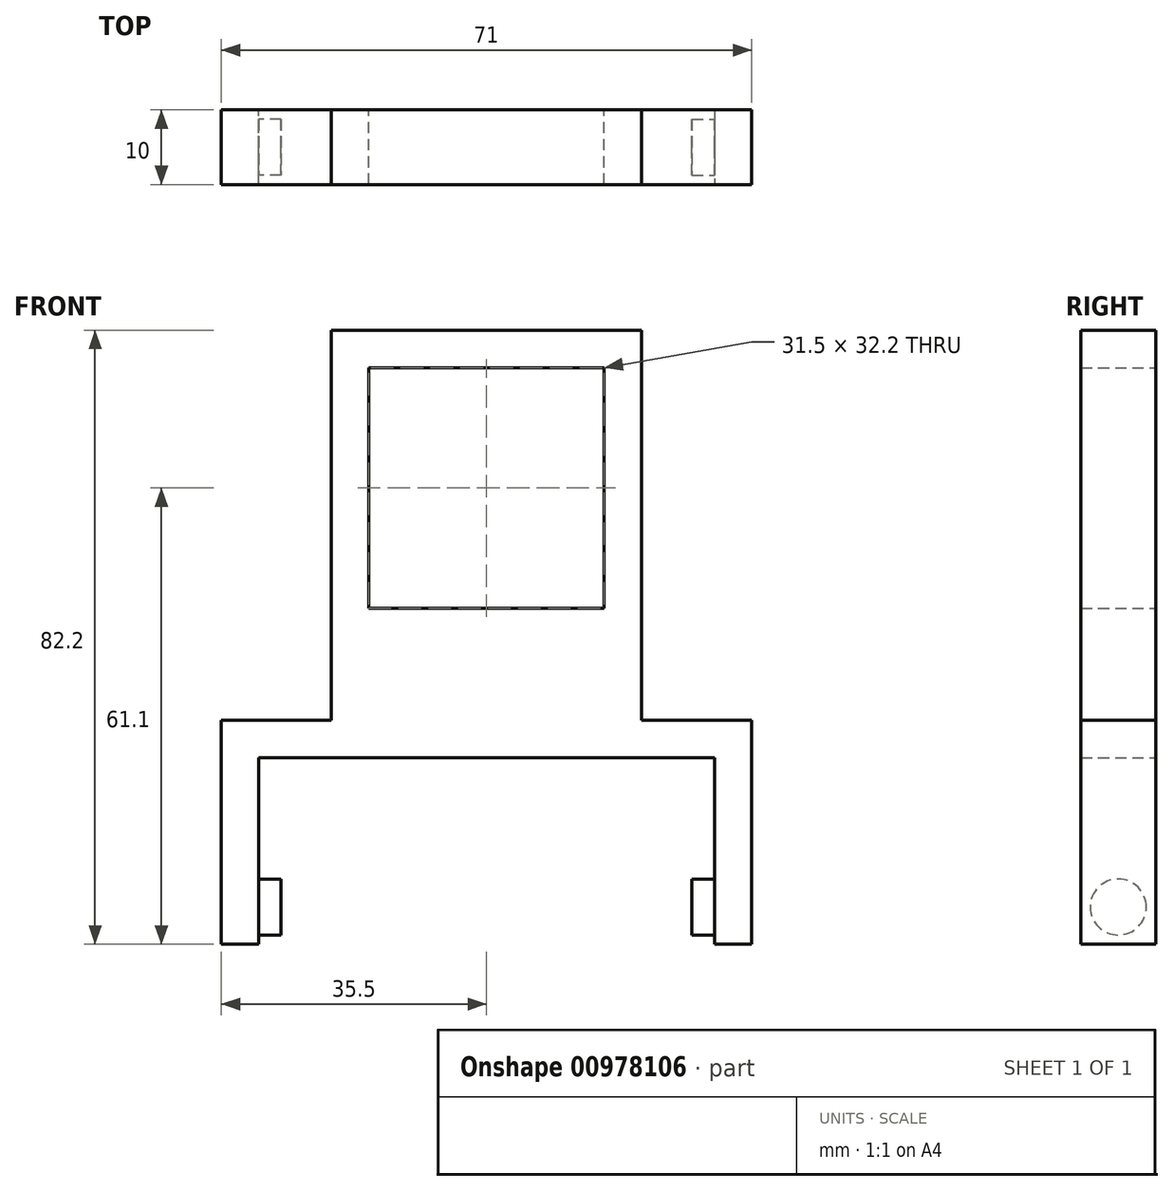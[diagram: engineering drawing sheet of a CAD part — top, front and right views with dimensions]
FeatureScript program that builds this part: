
annotation { "Feature Type Name" : "Feature", "Feature Type Description" : "" }
export const myFeature = defineFeature(function(context is Context, id is Id, definition is map)
    precondition{}
    {
        {
            var Q0;
            Q0=qCreatedBy(makeId("Front.planeOp"),FACE);
            var sketch = newSketch(context, id + "F0", { "sketchPlane" : qUnion([Q0])});
            skLineSegment(sketch, "E0.bottom", {"start": v(0, 0) * mm, "end": v(-31.5, 0) * mm});
            skLineSegment(sketch, "E0.top", {"start": v(0, 32.2) * mm, "end": v(-31.5, 32.2) * mm});
            skLineSegment(sketch, "E0.left", {"start": v(0, 0) * mm, "end": v(0, 32.2) * mm});
            skLineSegment(sketch, "E0.right", {"start": v(-31.5, 0) * mm, "end": v(-31.5, 32.2) * mm});
            skSolve(sketch);
        }
        {
            var Q0;
            Q0=qCreatedBy(makeId("Front.planeOp"),FACE);
            var sketch = newSketch(context, id + "F1", { "sketchPlane" : qUnion([Q0])});
            skLineSegment(sketch, "E1.bottom", {"start": v(-36.5, 37.2) * mm, "end": v(5, 37.2) * mm});
            skLineSegment(sketch, "E1.top", {"start": v(-36.5, -5) * mm, "end": v(5, -5) * mm});
            skLineSegment(sketch, "E1.left", {"start": v(-36.5, 37.2) * mm, "end": v(-36.5, -5) * mm});
            skLineSegment(sketch, "E1.right", {"start": v(5, 37.2) * mm, "end": v(5, -5) * mm});
            skSolve(sketch);
        }
        {
            var Q0;
            Q0=makeQuery(id+"F1.imprint","IMPRINT",FACE,{"disambiguationData":[TD([[makeQuery(id+"F1.imprint","IMPRINT",EDGE,{"derivedFrom":sQuery(id+"F1.wireOp",EDGE,"E1.bottom")}),-1.0]])]});
            extrude(context, id + "F2", {"entities" : qUnion([Q0]), "depth" : 10 * mm, "offsetDistance" : 25 * mm});
        }
        {
            var Q0;
            Q0=makeQuery(id+"F0.imprint","IMPRINT",FACE,{"disambiguationData":[TD([[makeQuery(id+"F0.imprint","IMPRINT",EDGE,{"derivedFrom":sQuery(id+"F0.wireOp",EDGE,"E0.bottom")}),-1.0]])]});
            extrude(context, id + "F3", {"entities" : qUnion([Q0]), "operationType" : NewBodyOperationType.REMOVE, "depth" : 25 * mm, "offsetDistance" : 25 * mm});
        }
        {
            var Q0;
            Q0=makeQuery(id+"F2.opExtrude","SWEPT_FACE",FACE,{"disambiguationData":[OSD([sQuery(id+"F1.wireOp",EDGE,"E1.top")])]});
            var sketch = newSketch(context, id + "F4", { "sketchPlane" : qUnion([Q0])});
            skLineSegment(sketch, "E2.bottom", {"start": v(5, 0) * mm, "end": v(0, 0) * mm});
            skLineSegment(sketch, "E2.top", {"start": v(5, 10) * mm, "end": v(0, 10) * mm});
            skLineSegment(sketch, "E2.left", {"start": v(5, 0) * mm, "end": v(5, 10) * mm});
            skLineSegment(sketch, "E2.right", {"start": v(0, 0) * mm, "end": v(0, 10) * mm});
            skLineSegment(sketch, "E3.bottom", {"start": v(-36.5, 0) * mm, "end": v(-31.5, 0) * mm});
            skLineSegment(sketch, "E3.top", {"start": v(-36.5, 10) * mm, "end": v(-31.5, 10) * mm});
            skLineSegment(sketch, "E3.left", {"start": v(-36.5, 0) * mm, "end": v(-36.5, 10) * mm});
            skLineSegment(sketch, "E3.right", {"start": v(-31.5, 0) * mm, "end": v(-31.5, 10) * mm});
            skSolve(sketch);
        }
        {
            var Q0;
            Q0 = qSketchRegion(id + "F4", true);
            extrude(context, id + "F5", {"entities" : qUnion([Q0]), "operationType" : NewBodyOperationType.ADD, "depth" : 10 * mm, "offsetDistance" : 25 * mm});
        }
        {
            var Q0;
            Q0=makeQuery(id+"F5.opExtrude","CAP_FACE",FACE,{"disambiguationData":[OSD([sQuery(id+"F4.wireOp",EDGE,"E2.bottom"),sQuery(id+"F4.wireOp",EDGE,"E2.top"),sQuery(id+"F4.wireOp",EDGE,"E2.left"),sQuery(id+"F4.wireOp",EDGE,"E2.right")])],"isStart":false});
            var sketch = newSketch(context, id + "F6", { "sketchPlane" : qUnion([Q0])});
            skLineSegment(sketch, "E4.bottom", {"start": v(19.75, 0) * mm, "end": v(-51.25, 0) * mm});
            skLineSegment(sketch, "E4.top", {"start": v(19.75, 10) * mm, "end": v(-51.25, 10) * mm});
            skLineSegment(sketch, "E4.left", {"start": v(19.75, 0) * mm, "end": v(19.75, 10) * mm});
            skLineSegment(sketch, "E4.right", {"start": v(-51.25, 0) * mm, "end": v(-51.25, 10) * mm});
            skSolve(sketch);
        }
        {
            var Q0;
            Q0 = qSketchRegion(id + "F6", true);
            extrude(context, id + "F7", {"entities" : qUnion([Q0]), "operationType" : NewBodyOperationType.ADD, "depth" : 5 * mm, "offsetDistance" : 25 * mm});
        }
        {
            var Q0;
            Q0=makeQuery(id+"F7.opExtrude","CAP_FACE",FACE,{"disambiguationData":[OSD([sQuery(id+"F6.wireOp",EDGE,"E4.bottom"),sQuery(id+"F6.wireOp",EDGE,"E4.top"),sQuery(id+"F6.wireOp",EDGE,"E4.left"),sQuery(id+"F6.wireOp",EDGE,"E4.right")])],"isStart":false});
            var sketch = newSketch(context, id + "F8", { "sketchPlane" : qUnion([Q0])});
            skLineSegment(sketch, "E5.bottom", {"start": v(19.75, 0) * mm, "end": v(14.75, 0) * mm});
            skLineSegment(sketch, "E5.top", {"start": v(19.75, 10) * mm, "end": v(14.75, 10) * mm});
            skLineSegment(sketch, "E5.left", {"start": v(19.75, 0) * mm, "end": v(19.75, 10) * mm});
            skLineSegment(sketch, "E5.right", {"start": v(14.75, 0) * mm, "end": v(14.75, 10) * mm});
            skLineSegment(sketch, "E6.bottom", {"start": v(-51.25, 10) * mm, "end": v(-46.25, 10) * mm});
            skLineSegment(sketch, "E6.top", {"start": v(-51.25, 0) * mm, "end": v(-46.25, 0) * mm});
            skLineSegment(sketch, "E6.left", {"start": v(-51.25, 10) * mm, "end": v(-51.25, 0) * mm});
            skLineSegment(sketch, "E6.right", {"start": v(-46.25, 10) * mm, "end": v(-46.25, 0) * mm});
            skSolve(sketch);
        }
        {
            var Q0;
            Q0 = qSketchRegion(id + "F8", true);
            extrude(context, id + "F9", {"entities" : qUnion([Q0]), "operationType" : NewBodyOperationType.ADD, "depth" : 25 * mm, "offsetDistance" : 25 * mm});
        }
        {
            var Q0;
            Q0=makeQuery(id+"F9.opExtrude","SWEPT_FACE",FACE,{"disambiguationData":[OSD([sQuery(id+"F8.wireOp",EDGE,"E5.right")])]});
            var sketch = newSketch(context, id + "F10", { "sketchPlane" : qUnion([Q0])});
            skCircle(sketch, "E7", {"center": v(5, -40) * mm, "radius": 3.75 * mm});
            skSolve(sketch);
        }
        {
            var Q0;
            Q0=makeQuery(id+"F9.opExtrude","SWEPT_FACE",FACE,{"disambiguationData":[OSD([sQuery(id+"F8.wireOp",EDGE,"E6.right")])]});
            var sketch = newSketch(context, id + "F11", { "sketchPlane" : qUnion([Q0])});
            skCircle(sketch, "E8", {"center": v(-5, -40) * mm, "radius": 3.75 * mm});
            skSolve(sketch);
        }
        {
            var Q0;
            Q0 = qSketchRegion(id + "F11", true);
            extrude(context, id + "F12", {"entities" : qUnion([Q0]), "operationType" : NewBodyOperationType.ADD, "depth" : 3 * mm, "offsetDistance" : 25 * mm});
        }
        {
            var Q0;
            Q0=makeQuery(id+"F9.boolean.opBoolean","MERGE",FACE,{"derivedFrom":[makeQuery(id+"F7.boolean.opBoolean","MERGE",FACE,{"derivedFrom":[makeQuery(id+"F5.boolean.opBoolean","MERGE",FACE,{"derivedFrom":[makeQuery(id+"F2.opExtrude","CAP_FACE",FACE,{"disambiguationData":[OSD([sQuery(id+"F1.wireOp",EDGE,"E1.bottom"),sQuery(id+"F1.wireOp",EDGE,"E1.top"),sQuery(id+"F1.wireOp",EDGE,"E1.left"),sQuery(id+"F1.wireOp",EDGE,"E1.right")])],"isStart":true}),makeQuery(id+"F5.opExtrude","SWEPT_FACE",FACE,{"disambiguationData":[OSD([sQuery(id+"F4.wireOp",EDGE,"E2.bottom")])]}),makeQuery(id+"F5.opExtrude","SWEPT_FACE",FACE,{"disambiguationData":[OSD([sQuery(id+"F4.wireOp",EDGE,"E3.bottom")])]})]}),makeQuery(id+"F7.opExtrude","SWEPT_FACE",FACE,{"disambiguationData":[OSD([sQuery(id+"F6.wireOp",EDGE,"E4.bottom")])]})]}),makeQuery(id+"F9.opExtrude","SWEPT_FACE",FACE,{"disambiguationData":[OSD([sQuery(id+"F8.wireOp",EDGE,"E5.bottom")])]}),makeQuery(id+"F9.opExtrude","SWEPT_FACE",FACE,{"disambiguationData":[OSD([sQuery(id+"F8.wireOp",EDGE,"E6.top")])]})]});
            var sketch = newSketch(context, id + "F13", { "sketchPlane" : qUnion([Q0])});
            skLineSegment(sketch, "E9.bottom", {"start": v(0, -15) * mm, "end": v(31.5, -15) * mm});
            skLineSegment(sketch, "E9.top", {"start": v(0, -5) * mm, "end": v(31.5, -5) * mm});
            skLineSegment(sketch, "E9.left", {"start": v(0, -15) * mm, "end": v(0, -5) * mm});
            skLineSegment(sketch, "E9.right", {"start": v(31.5, -15) * mm, "end": v(31.5, -5) * mm});
            skSolve(sketch);
        }
        {
            var Q0;
            Q0 = qSketchRegion(id + "F13", true);
            extrude(context, id + "F14", {"entities" : qUnion([Q0]), "operationType" : NewBodyOperationType.ADD, "oppositeDirection" : true, "depth" : 10 * mm, "offsetDistance" : 25 * mm});
        }
        {
            var Q0;
            Q0 = qSketchRegion(id + "F10", true);
            extrude(context, id + "F15", {"entities" : qUnion([Q0]), "operationType" : NewBodyOperationType.ADD, "depth" : 3 * mm, "offsetDistance" : 25 * mm});
        }
    });
